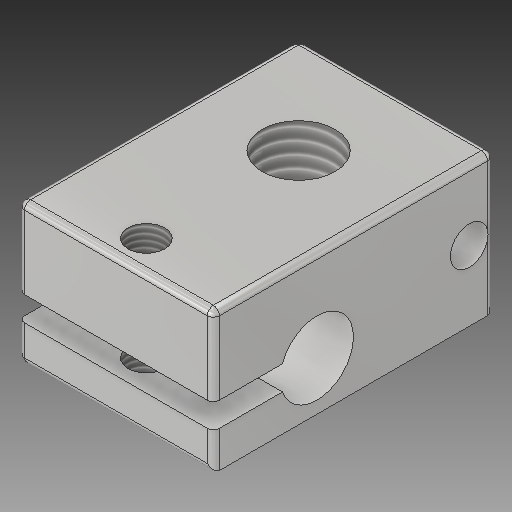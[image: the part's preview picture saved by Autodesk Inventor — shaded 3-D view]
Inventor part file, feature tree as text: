
AUTODESK INVENTOR PART (.ipt)
format: ipt  version: 2019 (Build 230136000, 136)  size: 236,544 bytes
history: native  units: mm
features: extrude x4, thread x4, sketch x4, fillet x1
ambient origin geometry x8: Origin, YZ Plane, XZ Plane, XY Plane, X Axis, Y Axis, Z Axis, Center Point
bodies: Solid1 (feature_tree)
feature tree (13):
  extrude  "Extrusion1"  Depth=23.0mm
  extrude  "Extrusion2"  Depth=14.5mm
  extrude  "Extrusion3"  Depth=4.0mm
  extrude  "Extrusion4"  Depth=2.0mm
  fillet  "Fillet1"  Radius=3.1mm
  thread  "Thread1"  [1 undecoded]
  thread  "Thread2"  [1 undecoded]
  thread  "Thread3"  [1 undecoded]
  thread  "Thread4"  [1 undecoded]
  sketch  "Sketch1"  dims[d0=16.0mm d1=23.0mm]
  sketch  "Sketch2"  dims[d2=11.5mm d3=0.0mm d4=14.5mm]
  sketch  "Sketch3"  dims[d5=6.0mm d6=4.0mm]
  sketch  "Sketch4"  dims[d7=8.5mm d8=2.0mm d9=3.1mm d10=2.0mm d11=5.74mm d12=11.5mm d13=0.0mm d14=8.0mm d15=6.0mm d17=20.5mm d18=3.0mm d19=0.0mm d20=0.0mm d21=3.0mm d22=2.0mm d23=11.5mm d24=0.0mm d25=0.5mm d26=10.0mm d27=0.0mm d28=10.0mm d29=0.0mm d30=10.0mm d31=0.0mm d32=10.0mm d33=0.0mm]
note: 4 required parameter values undecoded (feature->parameter linkage not recoverable at this tier; creation-order binding heuristic only, values carry confidence <= 0.55)
